# Revit family: GR_Адаптер линейный_Муфта(1)_Airslot-КСД_R21
name_source: partatom
category: Соединительные детали воздуховодов
units: mm (PartAtom-declared; Revit-internal decimal feet)

## family parameters
Всегда вертикально = Да
Заголовок OmniClass = Metal Ducts
На основе рабочей плоскости = Нет
Номер OmniClass = 23.75.70.14.31
Общий = Нет
При загрузке вырезать с полостями = Нет
Размер круглого соединителя = Использовать диаметр
Тип детали = Мультипорт

## types (18) — shared parameters
ADSK_URL страницы изделия = https://grilles.ru
ADSK_Версия Revit = 2021
ADSK_Единица измерения = шт.
ADSK_Завод-изготовитель = ООО "ВЕНТРЕШЕТКИКОМ"
ADSK_Код изделия = 000003
ADSK_Количество = 1
ADSK_Материал = ADSK_Оцинкованная сталь
ADSK_Наименование = Airslot-КСД, адаптер вентиляционной решётки
Изготовитель = ООО "ВЕНТРЕШЕТКИКОМ"
Корпус_Металл_Толщина = 1 мм
Муфта_Металл_Толщина = 1 мм
zero-valued in all types: Отметка по умолчанию

## per-type parameters (varying)
| type | Корпус_Высота | Корпус_Длина | Решётка_Высота | Решётка_Положение_Центр |
| Airslot-КСД 1-20 | 182 мм | 138 мм | 48 мм | 69 мм |
| Airslot-КСД 2-20 | 222 мм | 176 мм | 88 мм | 88 мм |
| Airslot-КСД 3-20 | 222 мм | 214 мм | 127 мм | 107 мм |
| Airslot-КСД 4-20 | 272 мм | 254 мм | 167 мм | 127 мм |
| Airslot-КСД 5-20 | 272 мм | 292 мм | 206 мм | 146 мм |
| Airslot-КСД 6-20 | 337 мм | 332 мм | 246 мм | 166 мм |
| Airslot-КСД 1-25 | 182 мм | 138 мм | 53 мм | 69 мм |
| Airslot-КСД 2-25 | 222 мм | 176 мм | 98 мм | 88 мм |
| Airslot-КСД 3-25 | 222 мм | 238 мм | 142 мм | 119 мм |
| Airslot-КСД 4-25 | 272 мм | 310 мм | 187 мм | 155 мм |
| Airslot-КСД 5-25 | 272 мм | 360 мм | 231 мм | 180 мм |
| Airslot-КСД 6-25 | 222 мм | 400 мм | 276 мм | 200 мм |
| Airslot-КСД 1-30 | 182 мм | 138 мм | 58 мм | 69 мм |
| Airslot-КСД 2-30 | 222 мм | 176 мм | 108 мм | 88 мм |
| Airslot-КСД 3-30 | 222 мм | 238 мм | 157 мм | 119 мм |
| Airslot-КСД 4-30 | 272 мм | 310 мм | 207 мм | 155 мм |
| Airslot-КСД 5-30 | 272 мм | 360 мм | 256 мм | 180 мм |
| Airslot-КСД 6-30 | 337 мм | 400 мм | 306 мм | 200 мм |

note: column(s) folded — value = type name in every type: ADSK_Марка
